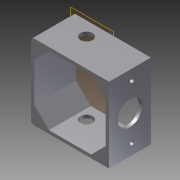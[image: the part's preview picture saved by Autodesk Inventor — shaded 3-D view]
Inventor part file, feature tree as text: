
AUTODESK INVENTOR PART (.ipt)
format: ipt  version: 2012 (Build 160160000, 160)  size: 142,336 bytes
history: native  units: in
note: dims shown in document units (in); Inventor stores cm internally (conversion verified against a paired STEP export)
features: reference x6, extrude x5, sketch x5, plane x2
ambient origin geometry x8: Origin, YZ Plane, XZ Plane, XY Plane, X Axis, Y Axis, Z Axis, Center Point
feature tree (18):
  plane  "Work Plane1"
  extrude  "Extrusion2"  Depth=0.5906in
  extrude  "Extrusion3"  Depth=0.2953in
  extrude  "Extrusion4"  Depth=1.0138in
  sketch  "Sketch7"  dims[d11=0.6759in d12=0.5906in]
  plane  "Work Plane2"
  extrude  "Extrusion5"  Depth=0.5906in
  extrude  "Extrusion6"  Depth=1.0138in TaperAngle=0.0deg
  sketch  "Sketch3"  dims[d2=1.0138in d3=0.0in d4=0.5906in]
  reference  "Reference3"
  reference  "Reference4"
  sketch  "Sketch5"  dims[d5=1.0138in d6=0.0in d7=0.2953in]
  sketch  "Sketch6"  dims[d8=1.0138in d9=0.0in d10=1.0138in]
  reference  "Reference5"
  reference  "Reference6"
  sketch  "Sketch8"  dims[d13=1.0138in d14=0.0in d15=1.0138in d16=0.0in]
  reference  "Reference7"
  reference  "Reference8"
